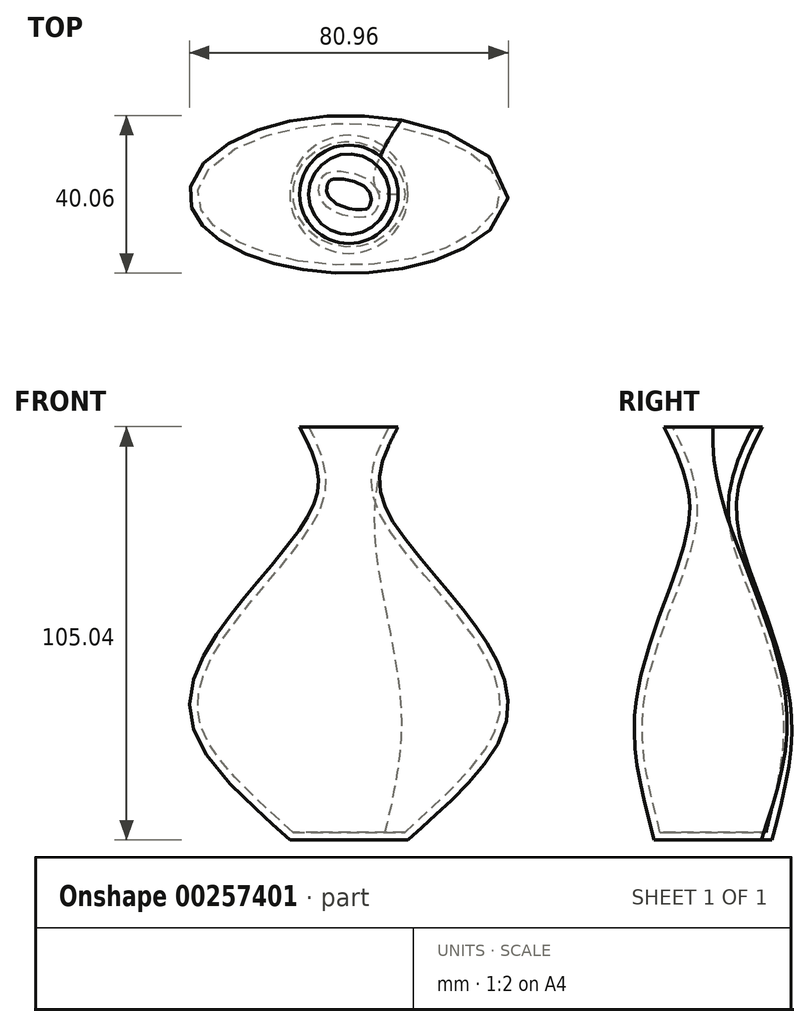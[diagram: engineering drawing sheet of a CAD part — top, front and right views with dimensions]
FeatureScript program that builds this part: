
annotation { "Feature Type Name" : "Feature", "Feature Type Description" : "" }
export const myFeature = defineFeature(function(context is Context, id is Id, definition is map)
    precondition{}
    {
        {
            var Q0;
            Q0=qCreatedBy(makeId("Top.planeOp"),FACE);
            var sketch = newSketch(context, id + "F0", { "sketchPlane" : qUnion([Q0])});
            skCircle(sketch, "E0", {"center": v(0, 0) * mm, "radius": 15 * mm});
            skSolve(sketch);
        }
        {
            var Q0;
            Q0=qCreatedBy(makeId("Top.planeOp"),FACE);
            cPlane(context, id + "F1", {"entities" : qUnion([Q0]), "cplaneType" : CPlaneType.OFFSET, "offset" : 30 * mm, "width" : 150 * mm, "height" : 150 * mm});
        }
        {
            var Q0;
            Q0=qCreatedBy(id+"F1.planeOp",FACE);
            var sketch = newSketch(context, id + "F2", { "sketchPlane" : qUnion([Q0])});
            skEllipse(sketch, "E1", {"center": v(0, 0) * mm, "majorRadius": 40 * mm, "minorRadius": 20 * mm, "majorAxis": v(1, 0)});
            skSolve(sketch);
        }
        {
            var Q0;
            Q0=qCreatedBy(id+"F1.planeOp",FACE);
            cPlane(context, id + "F3", {"entities" : qUnion([Q0]), "cplaneType" : CPlaneType.OFFSET, "offset" : 70 * mm, "width" : 150 * mm, "height" : 150 * mm});
        }
        {
            var Q0;
            Q0=qCreatedBy(id+"F3.planeOp",FACE);
            var sketch = newSketch(context, id + "F4", { "sketchPlane" : qUnion([Q0])});
            skCircle(sketch, "E2", {"center": v(0, 0) * mm, "radius": 10 * mm});
            skSolve(sketch);
        }
        {
            var Q0;
            Q0=qCreatedBy(id+"F3.planeOp",FACE);
            cPlane(context, id + "F5", {"entities" : qUnion([Q0]), "cplaneType" : CPlaneType.OFFSET, "offset" : 5 * mm, "width" : 150 * mm, "height" : 150 * mm});
        }
        {
            var Q0;
            Q0=qCreatedBy(id+"F5.planeOp",FACE);
            var sketch = newSketch(context, id + "F6", { "sketchPlane" : qUnion([Q0])});
            skCircle(sketch, "E3", {"center": v(0, 0) * mm, "radius": 12.5 * mm});
            skSolve(sketch);
        }
        {
            var Q0;
            Q0=makeQuery(id+"F6.imprint","IMPRINT",FACE,{"disambiguationData":[TD([[makeQuery(id+"F6.imprint","IMPRINT",EDGE,{"derivedFrom":sQuery(id+"F6.wireOp",EDGE,"E3")}),1.0]])]});
            var Q1;
            Q1=makeQuery(id+"F4.imprint","IMPRINT",FACE,{"disambiguationData":[TD([[makeQuery(id+"F4.imprint","IMPRINT",EDGE,{"derivedFrom":sQuery(id+"F4.wireOp",EDGE,"E2")}),1.0]])]});
            var Q2;
            Q2=makeQuery(id+"F2.imprint","IMPRINT",FACE,{"disambiguationData":[TD([[makeQuery(id+"F2.imprint","IMPRINT",EDGE,{"derivedFrom":sQuery(id+"F2.wireOp",EDGE,"E1")}),1.0]])]});
            var Q3;
            Q3=makeQuery(id+"F0.imprint","IMPRINT",FACE,{"disambiguationData":[TD([[makeQuery(id+"F0.imprint","IMPRINT",EDGE,{"derivedFrom":sQuery(id+"F0.wireOp",EDGE,"E0")}),1.0]])]});
            loft(context, id + "F7", {"sheetProfilesArray" : [{ "sheetProfileEntities" : qUnion([Q0]) }, { "sheetProfileEntities" : qUnion([Q1]) }, { "sheetProfileEntities" : qUnion([Q2]) }, { "sheetProfileEntities" : qUnion([Q3]) }]});
        }
        {
            var Q0;
            Q0=makeQuery(id+"F7.opLoft","CAP_FACE",FACE,{"disambiguationData":[OSD([makeQuery(id+"F6.imprint","IMPRINT",FACE,{"disambiguationData":[TD([[makeQuery(id+"F6.imprint","IMPRINT",EDGE,{"derivedFrom":sQuery(id+"F6.wireOp",EDGE,"E3")}),1.0]])]})])],"isStart":true});
            shell(context, id + "F8", {"entities" : qUnion([Q0]), "thickness" : 2 * mm});
        }
    });
